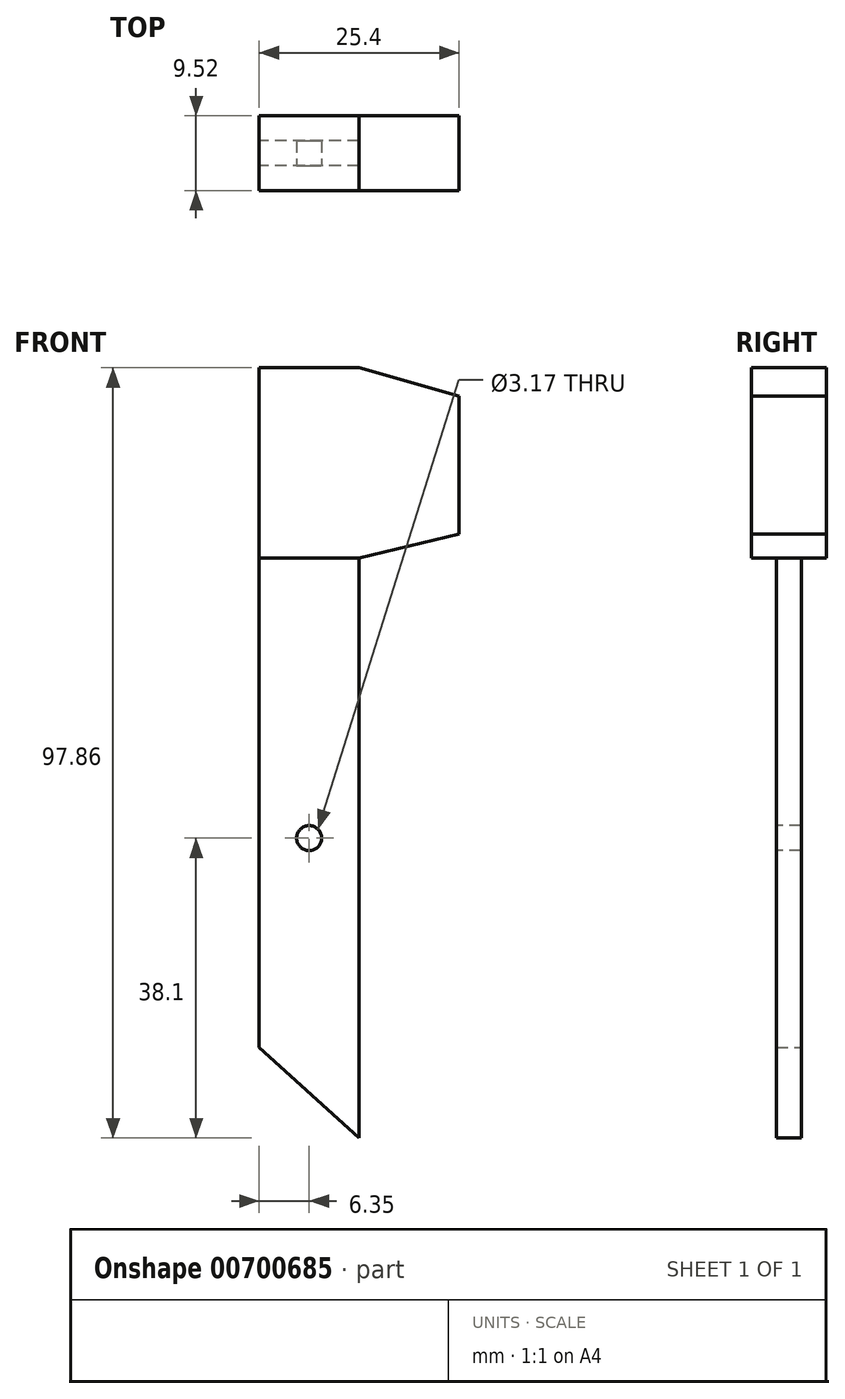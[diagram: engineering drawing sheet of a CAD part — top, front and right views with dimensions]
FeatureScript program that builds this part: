
annotation { "Feature Type Name" : "Feature", "Feature Type Description" : "" }
export const myFeature = defineFeature(function(context is Context, id is Id, definition is map)
    precondition{}
    {
        {
            var Q0;
            Q0=qCreatedBy(makeId("Front.planeOp"),FACE);
            var sketch = newSketch(context, id + "F0", { "sketchPlane" : qUnion([Q0])});
            skLineSegment(sketch, "E0", {"start": v(0, 0) * mm, "end": v(-12.7, 11.5) * mm});
            skLineSegment(sketch, "E1", {"start": v(-12.7, 11.5) * mm, "end": v(-12.7, 97.86) * mm});
            skLineSegment(sketch, "E2", {"start": v(-12.7, 97.86) * mm, "end": v(0, 97.86) * mm});
            skLineSegment(sketch, "E3", {"start": v(0, 0) * mm, "end": v(0, 73.66) * mm});
            skLineSegment(sketch, "E4", {"start": v(0, 73.66) * mm, "end": v(12.7, 76.75) * mm});
            skLineSegment(sketch, "E5", {"start": v(12.7, 76.75) * mm, "end": v(12.7, 94.23) * mm});
            skLineSegment(sketch, "E6", {"start": v(12.7, 94.23) * mm, "end": v(0, 97.86) * mm});
            skSolve(sketch);
        }
        {
            var Q0;
            Q0 = qSketchRegion(id + "F0", true);
            extrude(context, id + "F1", {"entities" : qUnion([Q0]), "depth" : 3.17 * mm, "offsetDistance" : 25.4 * mm});
        }
        {
            var Q0;
            Q0=makeQuery(id+"F1.opExtrude","CAP_FACE",FACE,{"disambiguationData":[OSD([sQuery(id+"F0.wireOp",EDGE,"E0"),sQuery(id+"F0.wireOp",EDGE,"E1"),sQuery(id+"F0.wireOp",EDGE,"E2"),sQuery(id+"F0.wireOp",EDGE,"E3"),sQuery(id+"F0.wireOp",EDGE,"E4"),sQuery(id+"F0.wireOp",EDGE,"E5"),sQuery(id+"F0.wireOp",EDGE,"E6")])],"isStart":false});
            var sketch = newSketch(context, id + "F2", { "sketchPlane" : qUnion([Q0])});
            skLineSegment(sketch, "E7.0", {"start": v(-12.7, 97.86) * mm, "end": v(0, 97.86) * mm});
            skLineSegment(sketch, "E8.0", {"start": v(12.7, 94.23) * mm, "end": v(0, 97.86) * mm});
            skLineSegment(sketch, "E9.0", {"start": v(12.7, 76.75) * mm, "end": v(12.7, 94.23) * mm});
            skLineSegment(sketch, "E10.0", {"start": v(0, 73.66) * mm, "end": v(12.7, 76.75) * mm});
            skLineSegment(sketch, "E11.0", {"start": v(-12.7, 73.66) * mm, "end": v(-12.7, 97.86) * mm});
            skLineSegment(sketch, "E12", {"start": v(0, 73.66) * mm, "end": v(-12.7, 73.66) * mm});
            skPoint(sketch, "E13.orphan", {"position": v(-12.7, 11.5) * mm});
            skSolve(sketch);
        }
        {
            var Q0;
            Q0 = qSketchRegion(id + "F2", true);
            extrude(context, id + "F3", {"entities" : qUnion([Q0]), "operationType" : NewBodyOperationType.ADD, "depth" : 3.17 * mm, "offsetDistance" : 25.4 * mm});
        }
        {
            var Q0;
            Q0=makeQuery(id+"F1.opExtrude","CAP_FACE",FACE,{"disambiguationData":[OSD([sQuery(id+"F0.wireOp",EDGE,"E0"),sQuery(id+"F0.wireOp",EDGE,"E1"),sQuery(id+"F0.wireOp",EDGE,"E2"),sQuery(id+"F0.wireOp",EDGE,"E3"),sQuery(id+"F0.wireOp",EDGE,"E4"),sQuery(id+"F0.wireOp",EDGE,"E5"),sQuery(id+"F0.wireOp",EDGE,"E6")])],"isStart":true});
            var sketch = newSketch(context, id + "F4", { "sketchPlane" : qUnion([Q0])});
            skLineSegment(sketch, "E14.0", {"start": v(0, 73.66) * mm, "end": v(-12.7, 76.75) * mm});
            skLineSegment(sketch, "E15.0", {"start": v(-12.7, 76.75) * mm, "end": v(-12.7, 94.23) * mm});
            skLineSegment(sketch, "E16.0", {"start": v(-12.7, 94.23) * mm, "end": v(0, 97.86) * mm});
            skLineSegment(sketch, "E17.0", {"start": v(12.7, 97.86) * mm, "end": v(0, 97.86) * mm});
            skLineSegment(sketch, "E18.0", {"start": v(12.7, 73.66) * mm, "end": v(12.7, 97.86) * mm});
            skLineSegment(sketch, "E19", {"start": v(0, 73.66) * mm, "end": v(12.7, 73.66) * mm});
            skPoint(sketch, "E20.orphan", {"position": v(12.7, 11.5) * mm});
            skSolve(sketch);
        }
        {
            var Q0;
            Q0 = qSketchRegion(id + "F4", true);
            extrude(context, id + "F5", {"entities" : qUnion([Q0]), "operationType" : NewBodyOperationType.ADD, "depth" : 3.17 * mm, "offsetDistance" : 25.4 * mm});
        }
        {
            var Q0;
            Q0=makeQuery(id+"F1.opExtrude","CAP_FACE",FACE,{"disambiguationData":[OSD([sQuery(id+"F0.wireOp",EDGE,"E0"),sQuery(id+"F0.wireOp",EDGE,"E1"),sQuery(id+"F0.wireOp",EDGE,"E2"),sQuery(id+"F0.wireOp",EDGE,"E3"),sQuery(id+"F0.wireOp",EDGE,"E4"),sQuery(id+"F0.wireOp",EDGE,"E5"),sQuery(id+"F0.wireOp",EDGE,"E6")])],"isStart":false});
            var sketch = newSketch(context, id + "F6", { "sketchPlane" : qUnion([Q0])});
            skPoint(sketch, "E21", {"position": v(-6.35, 21.66) * mm});
            skPoint(sketch, "E22", {"position": v(0, 21.66) * mm});
            skPoint(sketch, "E23", {"position": v(-12.7, 21.66) * mm});
            skSolve(sketch);
        }
        {
            var Q0;
            Q0=makeQuery(id+"F6.imprint","IMPRINT",FACE,{"disambiguationData":[TD([[makeQuery(id+"F6.imprint","IMPRINT",EDGE,{"derivedFrom":makeQuery(id+"F1.opExtrude","CAP_EDGE",EDGE,{"disambiguationData":[OSD([sQuery(id+"F0.wireOp",EDGE,"E0")])],"isStart":false})}),-1.0]])]});
            var sketch = newSketch(context, id + "F7", { "sketchPlane" : qUnion([Q0])});
            skPoint(sketch, "E24", {"position": v(-6.35, 38.1) * mm});
            skPoint(sketch, "E25", {"position": v(0, 38.1) * mm});
            skPoint(sketch, "E26", {"position": v(-12.7, 38.1) * mm});
            skSolve(sketch);
        }
        {
            var Q0;
            Q0=sQuery(id+"F7.wireOp",VERTEX,"E24");
            var Q1;
            Q1=makeQuery(id+"F1.opExtrude","SWEPT_BODY",BODY,{"disambiguationData":[OSD([sQuery(id+"F0.wireOp",EDGE,"E0"),sQuery(id+"F0.wireOp",EDGE,"E1"),sQuery(id+"F0.wireOp",EDGE,"E2"),sQuery(id+"F0.wireOp",EDGE,"E3"),sQuery(id+"F0.wireOp",EDGE,"E4"),sQuery(id+"F0.wireOp",EDGE,"E5"),sQuery(id+"F0.wireOp",EDGE,"E6")])]});
            hole(context, id + "F8", {"style" : HoleStyle.SIMPLE, "endStyle" : HoleEndStyle.THROUGH, "holeDiameter" : 3.17 * mm, "majorDiameter" : 6.35 * mm, "isTappedThrough" : true, "tappedDepth" : 12.7 * mm, "tapClearance" : 3, "startFromSketch" : true, "locations" : qUnion([Q0]), "scope" : qUnion([Q1])});
        }
    });
